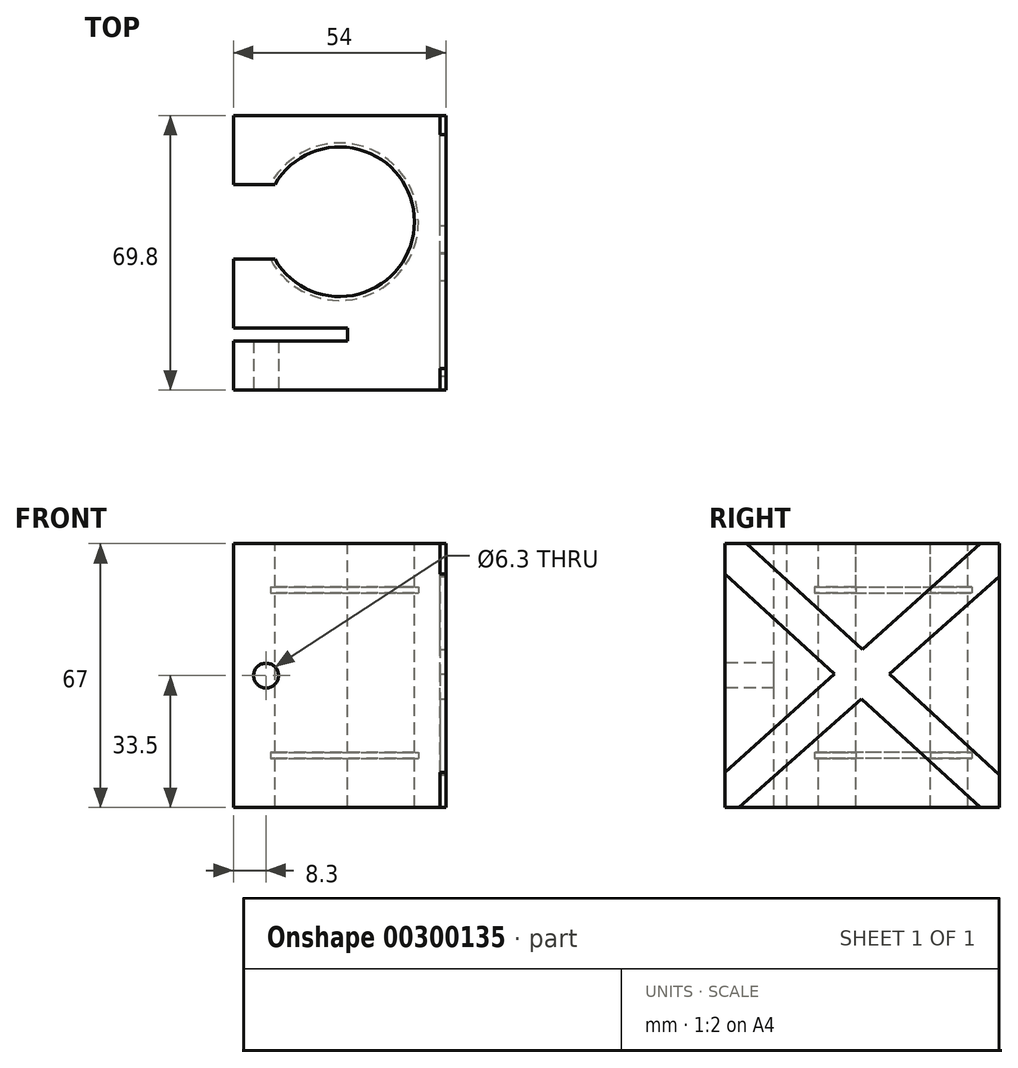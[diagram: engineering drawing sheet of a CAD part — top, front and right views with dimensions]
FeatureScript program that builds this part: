
annotation { "Feature Type Name" : "Feature", "Feature Type Description" : "" }
export const myFeature = defineFeature(function(context is Context, id is Id, definition is map)
    precondition{}
    {
        {
            var Q0;
            Q0=qCreatedBy(makeId("Front.planeOp"),FACE);
            var sketch = newSketch(context, id + "F0", { "sketchPlane" : qUnion([Q0])});
            skLineSegment(sketch, "E0.bottom", {"start": v(0, 0) * mm, "end": v(54, 0) * mm});
            skLineSegment(sketch, "E0.top", {"start": v(0, 67) * mm, "end": v(54, 67) * mm});
            skLineSegment(sketch, "E0.left", {"start": v(0, 0) * mm, "end": v(0, 67) * mm});
            skLineSegment(sketch, "E0.right", {"start": v(54, 0) * mm, "end": v(54, 67) * mm});
            skSolve(sketch);
        }
        {
            var Q0;
            Q0=makeQuery(id+"F0.imprint","IMPRINT",FACE,{"disambiguationData":[TD([[makeQuery(id+"F0.imprint","IMPRINT",EDGE,{"derivedFrom":sQuery(id+"F0.wireOp",EDGE,"E0.bottom")}),1.0]])]});
            extrude(context, id + "F1", {"entities" : qUnion([Q0]), "depth" : 69.8 * mm});
        }
        {
            var Q0;
            Q0=makeQuery(id+"F1.opExtrude","SWEPT_FACE",FACE,{"disambiguationData":[OSD([sQuery(id+"F0.wireOp",EDGE,"E0.top")])]});
            var sketch = newSketch(context, id + "F2", { "sketchPlane" : qUnion([Q0])});
            skArc(sketch, "E1", {"start": v(10.55, -36.5) * mm, "mid": v(46, -27) * mm, "end": v(10.55, -17.5) * mm});
            skLineSegment(sketch, "E2.bottom", {"start": v(10.55, -36.5) * mm, "end": v(0, -36.5) * mm});
            skLineSegment(sketch, "E2.top", {"start": v(10.55, -17.5) * mm, "end": v(0, -17.5) * mm});
            skLineSegment(sketch, "E2.right", {"start": v(0, -36.5) * mm, "end": v(0, -17.5) * mm});
            skPoint(sketch, "E3.start.orphan", {"position": v(27, -36.5) * mm});
            skLineSegment(sketch, "E4.bottom", {"start": v(29, -57.3) * mm, "end": v(0, -57.3) * mm});
            skLineSegment(sketch, "E4.top", {"start": v(29, -54) * mm, "end": v(0, -54) * mm});
            skLineSegment(sketch, "E4.left", {"start": v(29, -57.3) * mm, "end": v(29, -54) * mm});
            skSolve(sketch);
        }
        {
            var Q0;
            Q0=makeQuery(id+"F2.imprint","IMPRINT",FACE,{"disambiguationData":[TD([[makeQuery(id+"F2.imprint","IMPRINT",EDGE,{"derivedFrom":sQuery(id+"F2.wireOp",EDGE,"E1")}),1.0]])]});
            var Q1;
            {var subQ0=sQuery(id+"F2.wireOp",EDGE,"E4.bottom");Q1=makeQuery(id+"F2.imprint","IMPRINT",FACE,{"disambiguationData":[TD([[makeQuery(id+"F2.imprint","IMPRINT",EDGE,{"derivedFrom":subQ0}),-1.0]])]});}
            extrude(context, id + "F3", {"entities" : qUnion([Q0, Q1]), "operationType" : NewBodyOperationType.REMOVE, "oppositeDirection" : true, "depth" : 100 * mm});
        }
        {
            var Q0;
            Q0=makeQuery(id+"F1.opExtrude","SWEPT_FACE",FACE,{"disambiguationData":[OSD([sQuery(id+"F0.wireOp",EDGE,"E0.right")])]});
            var sketch = newSketch(context, id + "F4", { "sketchPlane" : qUnion([Q0])});
            skLineSegment(sketch, "E5", {"start": v(-69.8, 59.36) * mm, "end": v(-41.88, 33.86) * mm});
            skLineSegment(sketch, "E6", {"start": v(-64.26, 67) * mm, "end": v(-34.85, 40.14) * mm});
            skLineSegment(sketch, "E7", {"start": v(-69.8, 8.9) * mm, "end": v(-41.88, 33.86) * mm});
            skLineSegment(sketch, "E8", {"start": v(-66.2, 0) * mm, "end": v(-35.05, 27.62) * mm});
            skLineSegment(sketch, "E9", {"start": v(-69.8, 0) * mm, "end": v(-69.8, 8.9) * mm});
            skLineSegment(sketch, "E10", {"start": v(0, 58.69) * mm, "end": v(0, 67) * mm});
            skLineSegment(sketch, "E11", {"start": v(-4.8, 67) * mm, "end": v(0, 67) * mm});
            skLineSegment(sketch, "E12.trimOffspring", {"start": v(-35.05, 27.62) * mm, "end": v(-4.8, 0) * mm});
            skLineSegment(sketch, "E13.trimOffspring", {"start": v(-34.85, 40.14) * mm, "end": v(-4.8, 67) * mm});
            skLineSegment(sketch, "E14.trimOffspring", {"start": v(-28, 33.88) * mm, "end": v(0, 8.31) * mm});
            skLineSegment(sketch, "E15.trimOffspring", {"start": v(-28, 33.88) * mm, "end": v(0, 58.69) * mm});
            skSolve(sketch);
        }
        {
            var Q0;
            {var subQ3=sQuery(id+"F4.wireOp",EDGE,"E5");Q0=makeQuery(id+"F4.imprint","IMPRINT",FACE,{"disambiguationData":[TD([[makeQuery(id+"F4.imprint","IMPRINT",EDGE,{"derivedFrom":subQ3}),1.0]])]});}
            extrude(context, id + "F5", {"entities" : qUnion([Q0]), "operationType" : NewBodyOperationType.REMOVE, "oppositeDirection" : true, "depth" : 1.5 * mm});
        }
        {
            var Q0;
            Q0=makeQuery(id+"F1.opExtrude","CAP_FACE",FACE,{"disambiguationData":[OSD([sQuery(id+"F0.wireOp",EDGE,"E0.bottom"),sQuery(id+"F0.wireOp",EDGE,"E0.top"),sQuery(id+"F0.wireOp",EDGE,"E0.left"),sQuery(id+"F0.wireOp",EDGE,"E0.right")])],"isStart":false});
            var sketch = newSketch(context, id + "F6", { "sketchPlane" : qUnion([Q0])});
            skCircle(sketch, "E16", {"center": v(8.3, 33.5) * mm, "radius": 3.15 * mm});
            skSolve(sketch);
        }
        {
            var Q0;
            Q0=makeQuery(id+"F6.imprint","IMPRINT",FACE,{"disambiguationData":[TD([[makeQuery(id+"F6.imprint","IMPRINT",EDGE,{"derivedFrom":sQuery(id+"F6.wireOp",EDGE,"E16")}),1.0]])]});
            extrude(context, id + "F7", {"entities" : qUnion([Q0]), "operationType" : NewBodyOperationType.REMOVE, "oppositeDirection" : true, "depth" : 12.5 * mm});
        }
        {
            var Q0;
            Q0=makeQuery(id+"F1.opExtrude","SWEPT_FACE",FACE,{"disambiguationData":[OSD([sQuery(id+"F0.wireOp",EDGE,"E0.top")])]});
            cPlane(context, id + "F8", {"entities" : qUnion([Q0]), "cplaneType" : CPlaneType.OFFSET, "offset" : 12.5 * mm, "oppositeDirection" : true, "width" : 150 * mm, "height" : 150 * mm});
        }
        {
            var Q0;
            Q0=qCreatedBy(id+"F8.planeOp",FACE);
            var sketch = newSketch(context, id + "F9", { "sketchPlane" : qUnion([Q0])});
            skArc(sketch, "E17.0", {"start": v(10.55, -36.5) * mm, "mid": v(46, -27) * mm, "end": v(10.55, -17.5) * mm});
            skCircle(sketch, "E18", {"center": v(27, -27) * mm, "radius": 20 * mm});
            skSolve(sketch);
        }
        {
            var Q0;
            Q0 = qSketchRegion(id + "F9", true);
            extrude(context, id + "F10", {"entities" : qUnion([Q0]), "operationType" : NewBodyOperationType.REMOVE, "depth" : 1.5 * mm});
        }
        {
            var Q0;
            Q0=makeQuery(id+"F1.opExtrude","SWEPT_FACE",FACE,{"disambiguationData":[OSD([sQuery(id+"F0.wireOp",EDGE,"E0.bottom")])]});
            cPlane(context, id + "F11", {"entities" : qUnion([Q0]), "cplaneType" : CPlaneType.OFFSET, "offset" : 12.5 * mm, "oppositeDirection" : true, "width" : 150 * mm, "height" : 150 * mm});
        }
        {
            var Q0;
            Q0=qCreatedBy(id+"F11.planeOp",FACE);
            var sketch = newSketch(context, id + "F12", { "sketchPlane" : qUnion([Q0])});
            skArc(sketch, "E19.0", {"start": v(10.55, 36.5) * mm, "mid": v(46, 27) * mm, "end": v(10.55, 17.5) * mm});
            skCircle(sketch, "E20", {"center": v(27, 27) * mm, "radius": 20 * mm});
            skSolve(sketch);
        }
        {
            var Q0;
            Q0=makeQuery(id+"F12.imprint","IMPRINT",FACE,{"disambiguationData":[TD([[makeQuery(id+"F12.imprint","IMPRINT",EDGE,{"derivedFrom":sQuery(id+"F12.wireOp",EDGE,"E20")}),1.0]])]});
            extrude(context, id + "F13", {"entities" : qUnion([Q0]), "operationType" : NewBodyOperationType.REMOVE, "oppositeDirection" : true, "depth" : 1.5 * mm});
        }
    });
